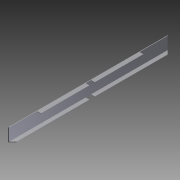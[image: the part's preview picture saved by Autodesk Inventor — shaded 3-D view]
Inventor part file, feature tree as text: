
AUTODESK INVENTOR PART (.ipt)
format: ipt  version: 2012 (Build 160160000, 160)  size: 114,176 bytes
history: native  units: in
note: dims shown in document units (in); Inventor stores cm internally (conversion verified against a paired STEP export)
features: extrude x4, sketch x3
ambient origin geometry x8: Origin, YZ Plane, XZ Plane, XY Plane, X Axis, Y Axis, Z Axis, Center Point
bodies: Solid1 (feature_tree)
feature tree (7):
  extrude  "Extrusion1"  Depth=1.0in
  sketch  "Sketch2"  dims[d2=0.125in d3=0.125in]
  extrude  "Extrusion2"  Depth=0.125in
  extrude  "Extrusion3"  Depth=37.0in TaperAngle=0.0deg
  extrude  "Extrusion4"  TaperAngle=45.0deg  [1 undecoded]
  sketch  "Sketch1"  dims[d0=3.0in d1=1.0in]
  sketch  "Sketch3"  dims[d4=0.125in d5=37.0in d6=0.0in d7=45.0deg d8=0.125in d9=6.5in d10=6.5in d11=28.0in d12=0.0in d13=28.0in d14=0.0in d15=1.25in d16=0.875in d17=17.875in d18=1.0in d19=0.0in]
note: 1 required parameter value undecoded (feature->parameter linkage not recoverable at this tier; creation-order binding heuristic only, values carry confidence <= 0.55)
